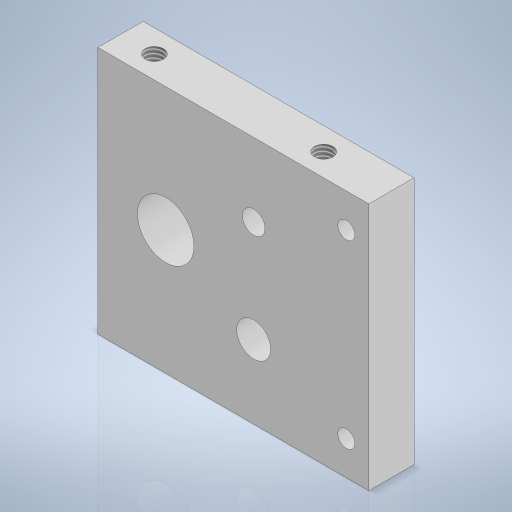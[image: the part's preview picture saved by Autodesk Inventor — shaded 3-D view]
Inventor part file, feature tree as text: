
AUTODESK INVENTOR PART (.ipt)
format: ipt  version: 2024 (Build 280153000, 153)  size: 272,384 bytes
history: native  units: mm
features: sketch x5, hole x3, extrude x2, plane x1, mirror x1
ambient origin geometry x8: Origin, YZ Plane, XZ Plane, XY Plane, X Axis, Y Axis, Z Axis, Center Point
bodies: Volumenkörper1 (feature_tree)
feature tree (12):
  extrude  "Extrusion1"  Depth=48.0mm
  extrude  "Extrusion2"  Depth=8.0mm
  hole  "Bohrung1"  [1 undecoded]
  hole  "Bohrung2"  [1 undecoded]
  hole  "Bohrung3"  [1 undecoded]
  plane  "Arbeitsebene1"
  mirror  "Spiegeln1"
  sketch  "Skizze1"  dims[d0=44.0mm d1=48.0mm]
  sketch  "Skizze2"  dims[d2=8.0mm d3=0.0mm d4=9.0mm]
  sketch  "Skizze3"  dims[d5=12.0mm d6=10.0mm]
  sketch  "Skizze4"  dims[d7=18.0mm d8=4.0mm]
  sketch  "Skizze5"  dims[d9=6.0mm d10=8.0mm d11=0.0mm d12=3.242mm d13=4.0mm d14=4.0mm d15=2.0mm d16=90.0deg d17=4.0mm d18=0.0mm d19=3.0mm d20=4.0mm d21=4.0mm d22=2.0mm d23=90.0deg d24=4.0mm d25=0.0mm d26=4.0mm d27=6.0mm d28=32.0mm d29=3.242mm d30=8.0mm d31=4.0mm d32=2.0mm d33=90.0deg d34=10.0mm d35=0.0mm d36=30.0mm d37=12.0mm d38=-22.0mm]
note: 3 required parameter values undecoded (feature->parameter linkage not recoverable at this tier; creation-order binding heuristic only, values carry confidence <= 0.55)
